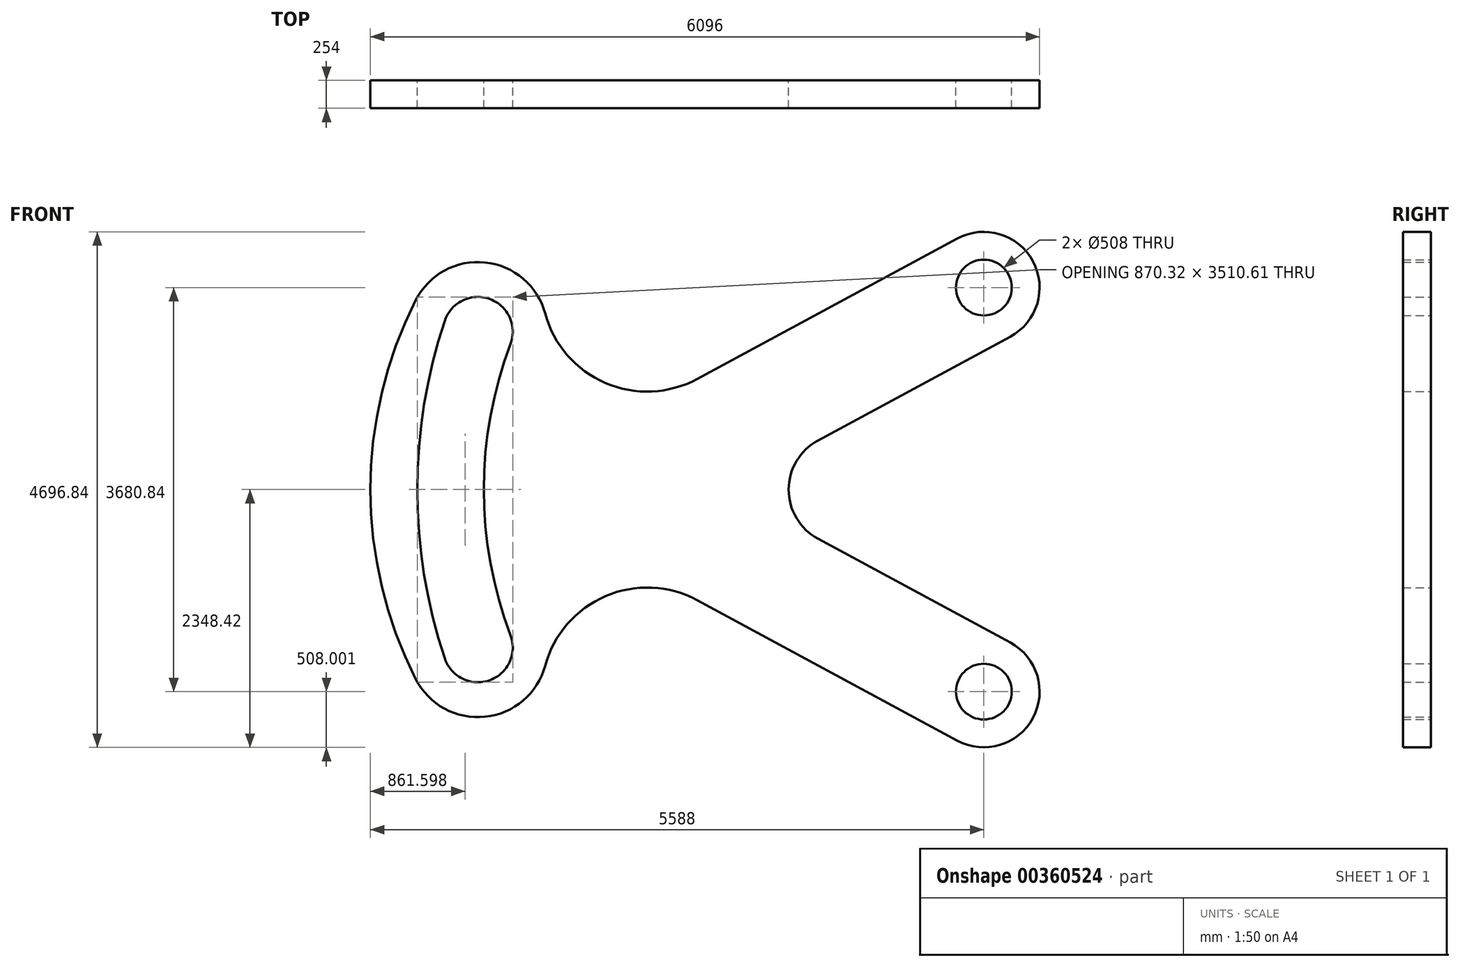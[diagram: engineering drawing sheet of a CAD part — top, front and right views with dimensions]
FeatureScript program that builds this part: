
annotation { "Feature Type Name" : "Feature", "Feature Type Description" : "" }
export const myFeature = defineFeature(function(context is Context, id is Id, definition is map)
    precondition{}
    {
        {
            var Q0;
            Q0=qCreatedBy(makeId("Front.planeOp"),FACE);
            var sketch = newSketch(context, id + "F0", { "sketchPlane" : qUnion([Q0])});
            skLineSegment(sketch, "E0", {"start": v(0, 0) * mm, "end": v(1917.7, 0) * mm, "construction": true});
            skArc(sketch, "E1", {"start": v(1676.33, 447) * mm, "mid": v(1409.7, 0) * mm, "end": v(1676.33, -447) * mm});
            skLineSegment(sketch, "E2", {"start": v(0, 0) * mm, "end": v(6375.4, 3680.84) * mm, "construction": true});
            skLineSegment(sketch, "E3", {"start": v(0, 0) * mm, "end": v(5063.52, -2923.43) * mm, "construction": true});
            skArc(sketch, "E4", {"start": v(3429.07, 1393.42) * mm, "mid": v(3634.7, 2081.79) * mm, "end": v(2946.33, 2287.42) * mm});
            skArc(sketch, "E5", {"start": v(2946.33, -2287.42) * mm, "mid": v(3634.7, -2081.79) * mm, "end": v(3429.07, -1393.42) * mm});
            skLineSegment(sketch, "E6", {"start": v(3429.07, 1393.42) * mm, "end": v(1676.33, 447) * mm});
            skLineSegment(sketch, "E7", {"start": v(3429.07, -1393.42) * mm, "end": v(1676.33, -447) * mm});
            skLineSegment(sketch, "E8", {"start": v(2946.33, -2287.42) * mm, "end": v(577.13, -1008.12) * mm});
            skLineSegment(sketch, "E9", {"start": v(2946.33, 2287.42) * mm, "end": v(577.13, 1008.12) * mm});
            skPoint(sketch, "E10.startSnap0", {"position": v(1409.7, 0) * mm});
            skArc(sketch, "E11", {"start": v(-1986.96, -1725.91) * mm, "mid": v(-2400.3, 0) * mm, "end": v(-1986.96, 1725.91) * mm});
            skArc(sketch, "E12", {"start": v(-807.77, 1603.64) * mm, "mid": v(-1355.36, 2069.88) * mm, "end": v(-1986.96, 1725.91) * mm});
            skArc(sketch, "E13", {"start": v(-1124.03, 1325.56) * mm, "mid": v(-1313.85, 1737.19) * mm, "end": v(-1721.77, 1539.53) * mm});
            skLineSegment(sketch, "E14", {"start": v(9314.86, 0) * mm, "end": v(-7208.14, 0) * mm, "construction": true});
            skArc(sketch, "E15.MirrorC", {"start": v(-807.77, -1603.64) * mm, "mid": v(-1355.36, -2069.88) * mm, "end": v(-1986.96, -1725.91) * mm});
            skArc(sketch, "E16.MirrorC", {"start": v(-1124.03, -1325.56) * mm, "mid": v(-1313.85, -1737.19) * mm, "end": v(-1721.77, -1539.53) * mm});
            skArc(sketch, "E17", {"start": v(-1721.77, 1539.53) * mm, "mid": v(-1973.86, 0) * mm, "end": v(-1721.77, -1539.53) * mm});
            skArc(sketch, "E18", {"start": v(-1124.03, 1325.56) * mm, "mid": v(-1367.2, 0) * mm, "end": v(-1124.03, -1325.56) * mm});
            skArc(sketch, "E19", {"start": v(-807.77, 1603.64) * mm, "mid": v(-259.37, 970.87) * mm, "end": v(577.13, 1008.12) * mm});
            skArc(sketch, "E20.MirrorCS", {"start": v(-807.77, -1603.64) * mm, "mid": v(-259.37, -970.87) * mm, "end": v(577.13, -1008.12) * mm});
            skPoint(sketch, "E21.orphan", {"position": v(1409.7, 3810) * mm});
            skPoint(sketch, "E22.orphan", {"position": v(1409.7, -3810) * mm});
            skCircle(sketch, "E23", {"center": v(3187.7, 1840.42) * mm, "radius": 254 * mm});
            skCircle(sketch, "E24", {"center": v(3187.7, -1840.42) * mm, "radius": 254 * mm});
            skSolve(sketch);
        }
        {
            var Q0;
            Q0=makeQuery(id+"F0.imprint","IMPRINT",FACE,{"disambiguationData":[TD([[makeQuery(id+"F0.imprint","IMPRINT",EDGE,{"derivedFrom":sQuery(id+"F0.wireOp",EDGE,"E1")}),-1.0]])]});
            extrude(context, id + "F1", {"entities" : qUnion([Q0]), "depth" : 254 * mm});
        }
    });
